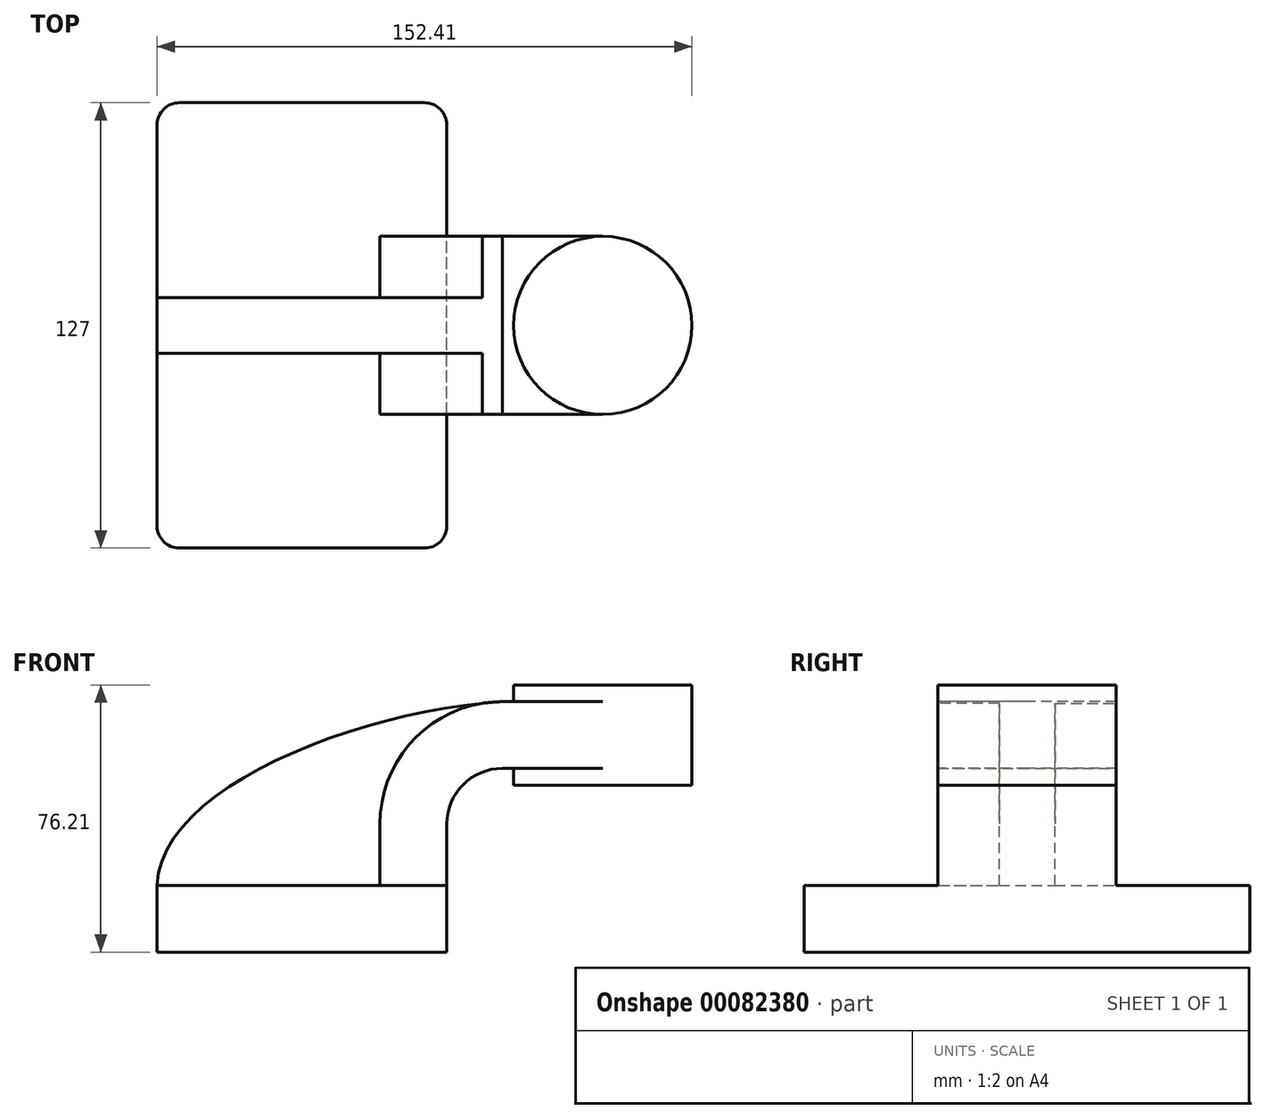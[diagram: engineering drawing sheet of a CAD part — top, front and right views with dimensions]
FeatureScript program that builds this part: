
annotation { "Feature Type Name" : "Feature", "Feature Type Description" : "" }
export const myFeature = defineFeature(function(context is Context, id is Id, definition is map)
    precondition{}
    {
        {
            var Q0;
            Q0=qCreatedBy(makeId("Front.planeOp"),FACE);
            var sketch = newSketch(context, id + "F0", { "sketchPlane" : qUnion([Q0])});
            skLineSegment(sketch, "E0.bottom", {"start": v(41.28, -9.53) * mm, "end": v(-41.28, -9.53) * mm});
            skLineSegment(sketch, "E0.top", {"start": v(41.28, 9.53) * mm, "end": v(-41.28, 9.52) * mm});
            skLineSegment(sketch, "E0.left", {"start": v(41.28, -9.52) * mm, "end": v(41.28, 9.53) * mm});
            skLineSegment(sketch, "E0.right", {"start": v(-41.28, -9.53) * mm, "end": v(-41.28, 9.52) * mm});
            skPoint(sketch, "E0.middle", {"position": v(0, 0) * mm});
            skLineSegment(sketch, "E1.bottom", {"start": v(111.12, 38.1) * mm, "end": v(60.32, 38.1) * mm});
            skLineSegment(sketch, "E1.top", {"start": v(111.12, 66.68) * mm, "end": v(60.32, 66.68) * mm});
            skLineSegment(sketch, "E1.left", {"start": v(111.12, 38.1) * mm, "end": v(111.12, 66.68) * mm});
            skLineSegment(sketch, "E1.right", {"start": v(60.32, 38.1) * mm, "end": v(60.32, 66.67) * mm});
            skPoint(sketch, "E1.middle", {"position": v(85.72, 52.39) * mm});
            skLineSegment(sketch, "E2", {"start": v(41.28, 9.53) * mm, "end": v(41.28, 27) * mm});
            skArc(sketch, "E3", {"start": v(41.27, 27) * mm, "mid": v(45.92, 38.23) * mm, "end": v(57.15, 42.88) * mm});
            skLineSegment(sketch, "E4", {"start": v(57.15, 42.88) * mm, "end": v(85.72, 42.88) * mm});
            skPoint(sketch, "E5", {"position": v(85.72, 38.1) * mm});
            skLineSegment(sketch, "E6.0", {"start": v(57.15, 61.93) * mm, "end": v(85.72, 61.93) * mm});
            skArc(sketch, "E6.1", {"start": v(22.22, 27) * mm, "mid": v(32.45, 51.7) * mm, "end": v(57.15, 61.93) * mm});
            skLineSegment(sketch, "E6.2", {"start": v(22.23, 9.53) * mm, "end": v(22.23, 27) * mm});
            skLineSegment(sketch, "E7", {"start": v(85.72, 38.1) * mm, "end": v(85.72, 66.68) * mm});
            skFitSpline(sketch, "E8", {"points": [v(-41.28, 9.52) * mm, v(57.15, 61.93) * mm], "startDerivative": vector(2.39, 84) * mm, "endDerivative": vector(122.33, 7.71) * mm});
            skSolve(sketch);
        }
        {
            var Q0;
            Q0=makeQuery(id+"F0.imprint","IMPRINT",FACE,{"disambiguationData":[TD([[makeQuery(id+"F0.imprint","IMPRINT",EDGE,{"derivedFrom":sQuery(id+"F0.wireOp",EDGE,"E0.bottom")}),-1.0]])]});
            extrude(context, id + "F1", {"entities" : qUnion([Q0]), "endBound" : BoundingType.SYMMETRIC, "depth" : 127 * mm});
        }
        {
            var Q0;
            {var subQ1=sQuery(id+"F0.wireOp",EDGE,"E2");Q0=makeQuery(id+"F0.imprint","IMPRINT",FACE,{"disambiguationData":[TD([[makeQuery(id+"F0.imprint","IMPRINT",EDGE,{"derivedFrom":subQ1}),1.0]])]});}
            var Q1;
            {var subQ0=sQuery(id+"F0.wireOp",EDGE,"E4");var subQ1=sQuery(id+"F0.wireOp",EDGE,"E1.right");var subQ2=makeQuery(id+"F0.imprint","INTERSECT",VERTEX,{"derivedFrom":[subQ1,subQ0]});Q1=makeQuery(id+"F0.imprint","IMPRINT",FACE,{"disambiguationData":[TD([[makeQuery(id+"F0.imprint","IMPRINT",EDGE,{"disambiguationData":[TD([[subQ2,-1.0]])],"derivedFrom":subQ1}),-1.0]])]});}
            extrude(context, id + "F2", {"entities" : qUnion([Q0, Q1]), "operationType" : NewBodyOperationType.ADD, "endBound" : BoundingType.SYMMETRIC, "depth" : 50.8 * mm});
        }
        {
            var Q0;
            {var subQ3=sQuery(id+"F0.wireOp",EDGE,"E6.2");Q0=makeQuery(id+"F0.imprint","IMPRINT",FACE,{"disambiguationData":[TD([[makeQuery(id+"F0.imprint","IMPRINT",EDGE,{"derivedFrom":subQ3}),1.0]])]});}
            extrude(context, id + "F3", {"entities" : qUnion([Q0]), "operationType" : NewBodyOperationType.ADD, "endBound" : BoundingType.SYMMETRIC, "depth" : 15.88 * mm});
        }
        {
            var Q0;
            {var subQ0=sQuery(id+"F0.wireOp",EDGE,"E1.left");Q0=makeQuery(id+"F0.imprint","IMPRINT",FACE,{"disambiguationData":[TD([[makeQuery(id+"F0.imprint","IMPRINT",EDGE,{"derivedFrom":subQ0}),1.0]])]});}
            var Q1;
            Q1=sQuery(id+"F0.wireOp",EDGE,"E7");
            revolve(context, id + "F4", {"operationType" : NewBodyOperationType.ADD, "entities" : qUnion([Q0]), "axis" : qUnion([Q1]), "revolveType" : RevolveType.FULL});
        }
        {
            var Q0;
            Q0=makeQuery(id+"F1.opExtrude","CAP_EDGE",EDGE,{"disambiguationData":[OSD([sQuery(id+"F0.wireOp",EDGE,"E0.left")])],"isStart":false});
            var Q1;
            Q1=makeQuery(id+"F1.opExtrude","CAP_EDGE",EDGE,{"disambiguationData":[OSD([sQuery(id+"F0.wireOp",EDGE,"E0.right")])],"isStart":false});
            var Q2;
            Q2=makeQuery(id+"F1.opExtrude","CAP_EDGE",EDGE,{"disambiguationData":[OSD([sQuery(id+"F0.wireOp",EDGE,"E0.left")])],"isStart":true});
            var Q3;
            Q3=makeQuery(id+"F1.opExtrude","CAP_EDGE",EDGE,{"disambiguationData":[OSD([sQuery(id+"F0.wireOp",EDGE,"E0.right")])],"isStart":true});
            fillet(context, id + "F5", {"entities" : qUnion([Q0, Q1, Q2, Q3]), "radius" : 6.35 * mm, "tangentPropagation" : true, "allowEdgeOverflow" : false});
        }
    });
